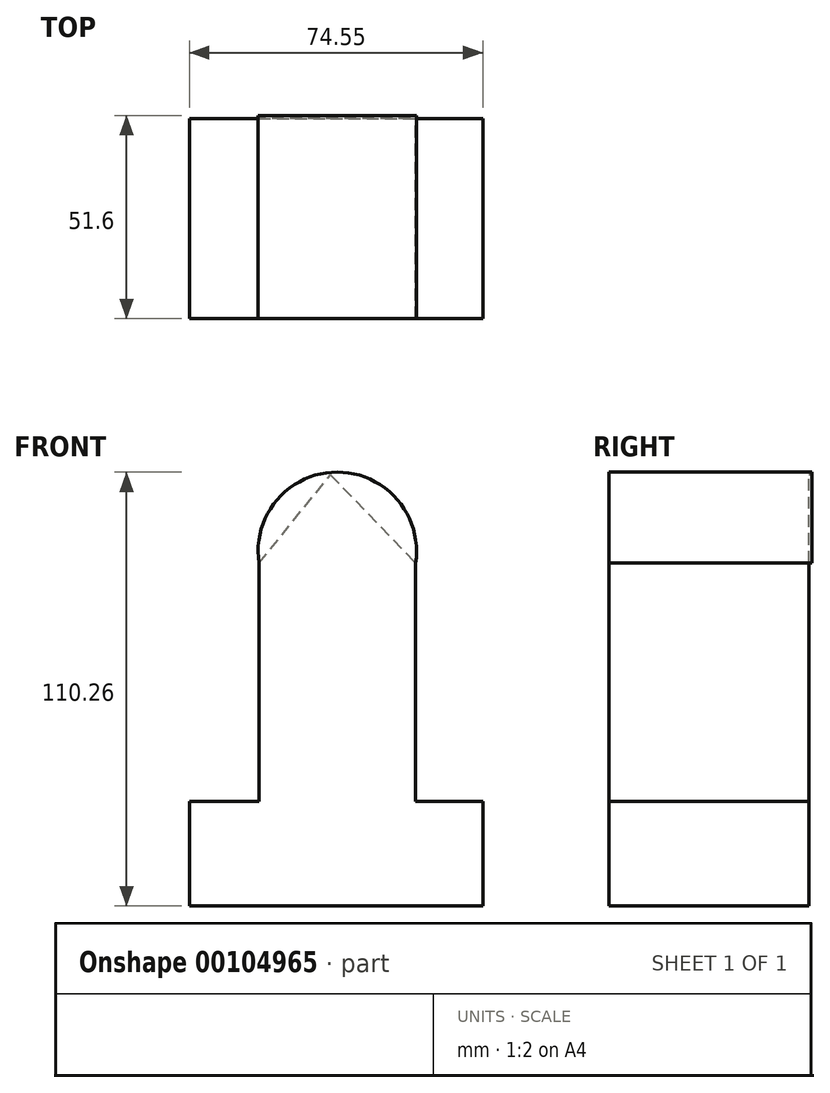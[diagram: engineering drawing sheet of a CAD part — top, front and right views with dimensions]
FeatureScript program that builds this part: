
annotation { "Feature Type Name" : "Feature", "Feature Type Description" : "" }
export const myFeature = defineFeature(function(context is Context, id is Id, definition is map)
    precondition{}
    {
        {
            var Q0;
            Q0=qCreatedBy(makeId("Front.planeOp"),FACE);
            var sketch = newSketch(context, id + "F0", { "sketchPlane" : qUnion([Q0])});
            skLineSegment(sketch, "E0", {"start": v(-44.56, -13.31) * mm, "end": v(-26.9, -13.31) * mm});
            skLineSegment(sketch, "E1", {"start": v(-26.9, -13.31) * mm, "end": v(-26.9, -39.93) * mm});
            skLineSegment(sketch, "E2", {"start": v(-26.9, -39.93) * mm, "end": v(-44.56, -39.93) * mm});
            skLineSegment(sketch, "E3", {"start": v(-44.56, -39.93) * mm, "end": v(-44.56, -13.31) * mm});
            skLineSegment(sketch, "E4", {"start": v(12.9, -13.31) * mm, "end": v(29.99, -13.31) * mm});
            skPoint(sketch, "E4.startSnap0", {"position": v(-35.73, -13.31) * mm});
            skLineSegment(sketch, "E5", {"start": v(29.99, -13.31) * mm, "end": v(29.99, -39.93) * mm});
            skLineSegment(sketch, "E6", {"start": v(29.99, -39.93) * mm, "end": v(12.9, -39.93) * mm});
            skLineSegment(sketch, "E7", {"start": v(12.9, -39.93) * mm, "end": v(12.9, -13.31) * mm});
            skLineSegment(sketch, "E8", {"start": v(-26.9, -13.31) * mm, "end": v(-26.9, 47.22) * mm});
            skLineSegment(sketch, "E9", {"start": v(-26.9, 47.22) * mm, "end": v(-8.69, 69.64) * mm});
            skLineSegment(sketch, "E10", {"start": v(-8.69, 69.64) * mm, "end": v(12.9, 47.22) * mm});
            skLineSegment(sketch, "E11", {"start": v(12.9, 47.22) * mm, "end": v(12.9, -13.31) * mm});
            skLineSegment(sketch, "E12", {"start": v(-26.9, -39.93) * mm, "end": v(12.9, -39.93) * mm});
            skSolve(sketch);
        }
        {
            var Q0;
            Q0 = qSketchRegion(id + "F0", true);
            extrude(context, id + "F1", {"entities" : qUnion([Q0]), "depth" : 50.8 * mm});
        }
        {
            var Q0;
            Q0=makeQuery(id+"F1.opExtrude","CAP_FACE",FACE,{"disambiguationData":[OSD([sQuery(id+"F0.wireOp",EDGE,"E0"),sQuery(id+"F0.wireOp",EDGE,"E2"),sQuery(id+"F0.wireOp",EDGE,"E3"),sQuery(id+"F0.wireOp",EDGE,"E4"),sQuery(id+"F0.wireOp",EDGE,"E5"),sQuery(id+"F0.wireOp",EDGE,"E6"),sQuery(id+"F0.wireOp",EDGE,"E8"),sQuery(id+"F0.wireOp",EDGE,"E9"),sQuery(id+"F0.wireOp",EDGE,"E10"),sQuery(id+"F0.wireOp",EDGE,"E11"),sQuery(id+"F0.wireOp",EDGE,"E12")])],"isStart":false});
            var sketch = newSketch(context, id + "F2", { "sketchPlane" : qUnion([Q0])});
            skArc(sketch, "E13", {"start": v(12.9, 47.22) * mm, "mid": v(-7, 70.33) * mm, "end": v(-26.9, 47.22) * mm});
            skSolve(sketch);
        }
        {
            var Q0;
            Q0 = qSketchRegion(id + "F2", true);
            var Q1;
            Q1=makeQuery(id+"F2.imprint","IMPRINT",FACE,{"disambiguationData":[TD([[makeQuery(id+"F2.imprint","IMPRINT",EDGE,{"derivedFrom":sQuery(id+"F2.wireOp",EDGE,"E13")}),1.0]])]});
            extrude(context, id + "F3", {"entities" : qUnion([Q0, Q1]), "operationType" : NewBodyOperationType.ADD, "oppositeDirection" : true, "depth" : 51.6 * mm});
        }
    });
